# Revit family: Hajom Classic Typ A - W001 (Wooden).0001 (1)
name_source: partatom
category: Doors
revit_build: Autodesk Revit 2016 (Build: 20150220_1215(x64)
units: mm (PartAtom-declared; Revit-internal decimal feet)

## family parameters
Always vertical = Yes
Cut with Voids When Loaded = No
Host = Wall
OmniClass Number = 23.30.10.00
OmniClass Title = Doors
Room Calculation Point = No
Shared = No

## types (1)
- Hajom Classic Typ A - W001 (Wooden).0001 (1)
    Analytic Construction = <None>
    BIMobject category = Sliding
    BIMobject category code = doors-sliding
    BIMobject main category = Doors
    BIMobject main category code = doors
    Brand url = https://hajom.com
    Design country = Sweden
    Door Image = Wood Brw.png
    Edition number = 1
    Frame Projection Ext. = 25 mm  [stored 0.082021 ft]
    Frame Projection Int. = 25 mm  [stored 0.082021 ft]
    Frame Width = 75 mm  [stored 0.246063 ft]
    Function = Interior
    Height = 0 mm  [stored 0 ft]
    IFC Classification = Door
    Installation instructions = http://www.hajom.com
    Manufacturer = HAJOM
    Manufacturer country = Sweden
    Manufacturer name = Hajom
    Masterformat 2014 Code = 08 32 19
    Masterformat 2014 Description = Sliding Wood-Framed Glass Doors
    Material main = Wood
    Material secondary = Glass
    Max Door Height = 2420 mm
    Max Door Width = 4380 mm
    Min Door Height = 2020 mm
    Min Door Width = 1780 mm
    Model = Hajom Cassic Typ A Wooden
    NBS Reference Code = 25-30-20-77
    NBS Reference Description = Sliding Doorset Systems
    Nominal height = 0 mm  [stored 0 ft]
    Nominal width = 0 mm  [stored 0 ft]
    OmniClass Code = 23-13 33 11
    OmniClass Description = Sliding Glass Wall Systems
    Product Guid = c40bfc95-3981-41ae-8295-8f9c89cbb009
    Product SKU = TypA
    Product certification = http://www.hajom.com
    Product data url = https://bimobject.com
    Product family = Skjutdörrar
    Product group = Klassiska
    Product url = http://www.hajom.com
    QR code = http://bimobject.com
    Rough Height = 0 mm  [stored 0 ft]
    Rough Width = 0 mm  [stored 0 ft]
    Technical description = http://www.hajom.com
    Thickness = 0 mm  [stored 0 ft]
    Type Comments = HAJOM ARCHITECT SERIES SLIDING DOORS
    Type Image = <None>
    UNSPSC Code = 301715
    URL = http://www.hajom.com
    Uniclass 1.4 Code = L41
    Uniclass 1.4 Description = Doors, windows, etc. (access products)
    Uniclass 2.0 Code = PR-59-23-77
    Uniclass 2.0 Description = Sliding Door And Partition Sets
    Uniclass 2015 Code = Ss_25_30_20_77
    Uniclass 2015 Name = Sliding doorset systems
    Uniformat II Code = B2030
    Uniformat II Description = Exterior Doors
    Wall Closure = By host
    Weight Net (Kg) = 0
    Width = 0 mm  [stored 0 ft]

note: [stored X ft] marks values corroborated as IEEE doubles in the binary element streams (Revit-internal decimal feet)

## geometry (parser evidence)
native form markers: Blend x6, Sweep x17
no freeform markers — native parametric forms only
